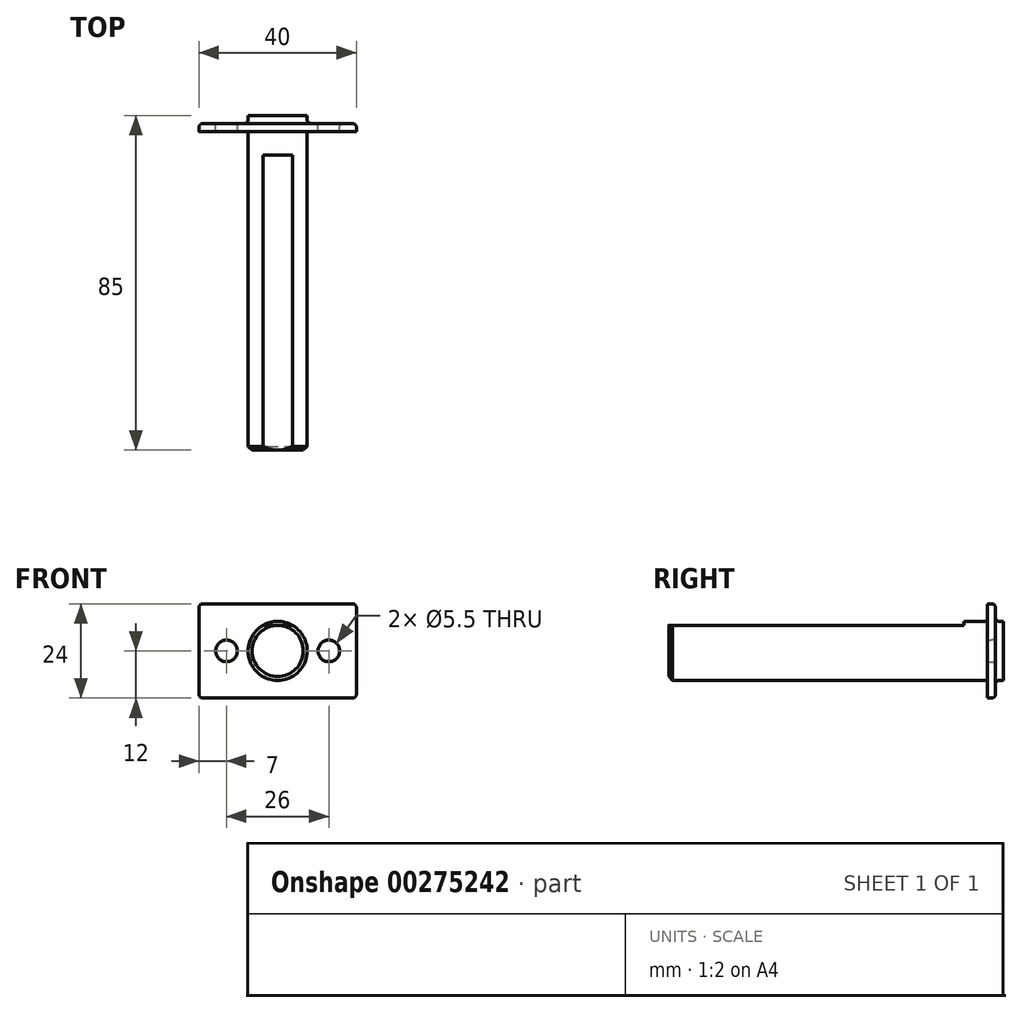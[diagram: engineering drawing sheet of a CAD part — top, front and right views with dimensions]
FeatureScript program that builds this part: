
annotation { "Feature Type Name" : "Feature", "Feature Type Description" : "" }
export const myFeature = defineFeature(function(context is Context, id is Id, definition is map)
    precondition{}
    {
        {
            var Q0;
            Q0=qCreatedBy(makeId("Front.planeOp"),FACE);
            var sketch = newSketch(context, id + "F0", { "sketchPlane" : qUnion([Q0])});
            skLineSegment(sketch, "E0.bottom", {"start": v(0, 0) * mm, "end": v(40, 0) * mm});
            skLineSegment(sketch, "E0.top", {"start": v(0, 24) * mm, "end": v(40, 24) * mm});
            skLineSegment(sketch, "E0.left", {"start": v(0, 0) * mm, "end": v(0, 24) * mm});
            skLineSegment(sketch, "E0.right", {"start": v(40, 0) * mm, "end": v(40, 24) * mm});
            skCircle(sketch, "E1", {"center": v(20, 12) * mm, "radius": 7.5 * mm});
            skPoint(sketch, "E1.centerSnap0", {"position": v(0, 12) * mm});
            skPoint(sketch, "E1.centerSnap1", {"position": v(20, 24) * mm});
            skCircle(sketch, "E2", {"center": v(33, 12) * mm, "radius": 2.5 * mm});
            skCircle(sketch, "E3", {"center": v(7, 12) * mm, "radius": 2.5 * mm});
            skLineSegment(sketch, "E4", {"start": v(20, 12) * mm, "end": v(20, 31.3) * mm, "construction": true});
            skSolve(sketch);
        }
        {
            var Q0;
            Q0=makeQuery(id+"F0.imprint","IMPRINT",FACE,{"disambiguationData":[TD([[makeQuery(id+"F0.imprint","IMPRINT",EDGE,{"derivedFrom":sQuery(id+"F0.wireOp",EDGE,"E1")}),1.0]])]});
            var Q1;
            Q1=makeQuery(id+"F0.imprint","IMPRINT",FACE,{"disambiguationData":[TD([[makeQuery(id+"F0.imprint","IMPRINT",EDGE,{"derivedFrom":sQuery(id+"F0.wireOp",EDGE,"E3")}),1.0]])]});
            var Q2;
            Q2=makeQuery(id+"F0.imprint","IMPRINT",FACE,{"disambiguationData":[TD([[makeQuery(id+"F0.imprint","IMPRINT",EDGE,{"derivedFrom":sQuery(id+"F0.wireOp",EDGE,"E2")}),1.0]])]});
            var Q3;
            Q3=makeQuery(id+"F0.imprint","IMPRINT",FACE,{"disambiguationData":[TD([[makeQuery(id+"F0.imprint","IMPRINT",EDGE,{"derivedFrom":sQuery(id+"F0.wireOp",EDGE,"E0.bottom")}),1.0]])]});
            extrude(context, id + "F1", {"entities" : qUnion([Q0, Q1, Q2, Q3]), "oppositeDirection" : true, "depth" : 4 * mm});
        }
        {
            var Q0;
            Q0=qCreatedBy(makeId("Front.planeOp"),FACE);
            var sketch = newSketch(context, id + "F2", { "sketchPlane" : qUnion([Q0])});
            skSolve(sketch);
        }
        {
            var Q0;
            Q0 = qSketchRegion(id + "F2", true);
            var Q1;
            Q1=makeQuery(id+"F0.imprint","IMPRINT",FACE,{"disambiguationData":[TD([[makeQuery(id+"F0.imprint","IMPRINT",EDGE,{"derivedFrom":sQuery(id+"F0.wireOp",EDGE,"E1")}),1.0]])]});
            extrude(context, id + "F3", {"entities" : qUnion([Q0, Q1]), "operationType" : NewBodyOperationType.ADD, "depth" : 81 * mm});
        }
        {
            var Q0;
            Q0=sQuery(id+"F0.wireOp",VERTEX,"E2.center");
            var Q1;
            Q1=sQuery(id+"F0.wireOp",VERTEX,"E3.center");
            var Q2;
            Q2=makeQuery(id+"F1.opExtrude","SWEPT_BODY",BODY,{"disambiguationData":[OSD([sQuery(id+"F0.wireOp",EDGE,"E0.bottom"),sQuery(id+"F0.wireOp",EDGE,"E0.top"),sQuery(id+"F0.wireOp",EDGE,"E0.left"),sQuery(id+"F0.wireOp",EDGE,"E0.right")])]});
            hole(context, id + "F4", {"style" : HoleStyle.SIMPLE, "endStyle" : HoleEndStyle.BLIND, "standardTappedOrClearance" : lookupTablePath({ "standard" : "ISO", "fit" : "Normal", "size" : "M5", "type" : "Clearance" }), "standardBlindInLast" : lookupTablePath({ "fit" : "Standard", "standard" : "ISO", "size" : "M5", "type" : "Clearance" }), "holeDiameter" : 5.5 * mm, "holeDepth" : 4 * mm, "tappedDepth" : 12 * mm, "tapClearance" : 3, "startFromSketch" : true, "locations" : qUnion([Q0, Q1]), "scope" : qUnion([Q2])});
        }
        {
            var Q0;
            Q0=makeQuery(id+"F3.opExtrude","CAP_FACE",FACE,{"disambiguationData":[OSD([sQuery(id+"F0.wireOp",EDGE,"E1")])],"isStart":false});
            var sketch = newSketch(context, id + "F5", { "sketchPlane" : qUnion([Q0])});
            skLineSegment(sketch, "E5", {"start": v(16.26, 18.5) * mm, "end": v(23.74, 18.5) * mm});
            skArc(sketch, "E6.0", {"start": v(23.74, 18.5) * mm, "mid": v(20, 19.5) * mm, "end": v(16.26, 18.5) * mm});
            skSolve(sketch);
        }
        {
            var Q0;
            Q0 = qSketchRegion(id + "F5", true);
            extrude(context, id + "F6", {"entities" : qUnion([Q0]), "operationType" : NewBodyOperationType.REMOVE, "oppositeDirection" : true, "depth" : 75 * mm});
        }
        {
            var Q0;
            Q0=makeQuery(id+"F3.opExtrude","CAP_EDGE",EDGE,{"disambiguationData":[OSD([sQuery(id+"F0.wireOp",EDGE,"E1")])],"isStart":false});
            chamfer(context, id + "F7", {"entities" : qUnion([Q0]), "chamferType" : ChamferType.OFFSET_ANGLE, "width" : 1 * mm, "oppositeDirection" : false, "angle" : 45 * degree, "tangentPropagation" : true});
        }
        {
            var Q0;
            Q0=makeQuery(id+"F1.opExtrude","CAP_FACE",FACE,{"disambiguationData":[OSD([sQuery(id+"F0.wireOp",EDGE,"E0.bottom"),sQuery(id+"F0.wireOp",EDGE,"E0.top"),sQuery(id+"F0.wireOp",EDGE,"E0.left"),sQuery(id+"F0.wireOp",EDGE,"E0.right")])],"isStart":false});
            var sketch = newSketch(context, id + "F8", { "sketchPlane" : qUnion([Q0])});
            skCircle(sketch, "E7.0", {"center": v(-20, 12) * mm, "radius": 7.5 * mm});
            skSolve(sketch);
        }
        {
            var Q0;
            Q0=makeQuery(id+"F8.imprint","IMPRINT",FACE,{"disambiguationData":[TD([[makeQuery(id+"F8.imprint","IMPRINT",EDGE,{"derivedFrom":sQuery(id+"F8.wireOp",EDGE,"E7.0")}),-1.0]])]});
            extrude(context, id + "F9", {"entities" : qUnion([Q0]), "operationType" : NewBodyOperationType.REMOVE, "oppositeDirection" : true, "depth" : 2 * mm});
        }
        {
            var Q0;
            Q0=makeQuery(id+"F1.opExtrude","SWEPT_EDGE",EDGE,{"disambiguationData":[OSD([sQuery(id+"F0.wireOp",EDGE,"E0.top"),sQuery(id+"F0.wireOp",EDGE,"E0.left")])]});
            var Q1;
            Q1=makeQuery(id+"F1.opExtrude","SWEPT_EDGE",EDGE,{"disambiguationData":[OSD([sQuery(id+"F0.wireOp",EDGE,"E0.bottom"),sQuery(id+"F0.wireOp",EDGE,"E0.left")])]});
            var Q2;
            Q2=makeQuery(id+"F1.opExtrude","SWEPT_EDGE",EDGE,{"disambiguationData":[OSD([sQuery(id+"F0.wireOp",EDGE,"E0.bottom"),sQuery(id+"F0.wireOp",EDGE,"E0.right")])]});
            var Q3;
            Q3=makeQuery(id+"F1.opExtrude","SWEPT_EDGE",EDGE,{"disambiguationData":[OSD([sQuery(id+"F0.wireOp",EDGE,"E0.top"),sQuery(id+"F0.wireOp",EDGE,"E0.right")])]});
            var Q4;
            Q4=makeQuery(id+"F9.boolean.opBoolean","COPY",FACE,{"derivedFrom":makeQuery(id+"F9.opExtrude","CAP_FACE",FACE,{"disambiguationData":[OSD([sQuery(id+"F8.wireOp",EDGE,"E7.0")])],"isStart":false})});
            fillet(context, id + "F10", {"entities" : qUnion([Q0, Q1, Q2, Q3, Q4]), "radius" : 1 * mm, "tangentPropagation" : true, "allowEdgeOverflow" : false});
        }
    });
